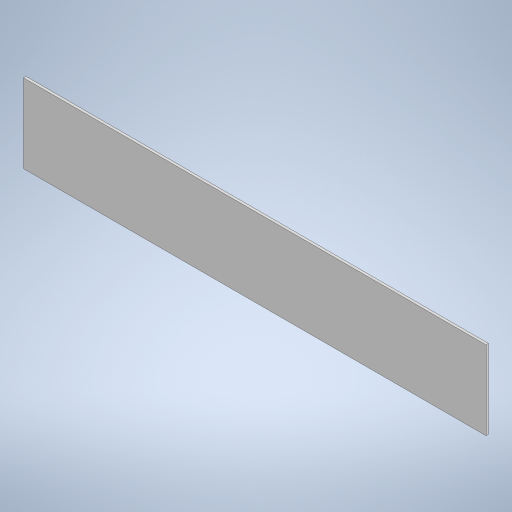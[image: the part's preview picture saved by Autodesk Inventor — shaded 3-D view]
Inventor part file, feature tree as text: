
AUTODESK INVENTOR PART (.ipt)
format: ipt  version: 2023 (Build 270158000, 158)  size: 214,016 bytes
history: native  units: mm
features: other x1, extrude x1, sketch x1
ambient origin geometry x8: Origin, YZ Plane, XZ Plane, XY Plane, X Axis, Y Axis, Z Axis, Center Point
bodies: Body1 (feature_tree)
feature tree (3):
  other  "ソリッド1"
  extrude  "押し出し1"  Depth=294.0mm
  sketch  "スケッチ1"
